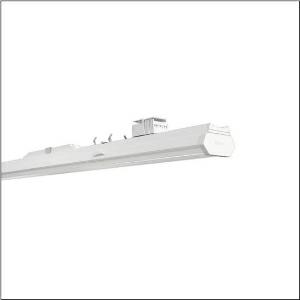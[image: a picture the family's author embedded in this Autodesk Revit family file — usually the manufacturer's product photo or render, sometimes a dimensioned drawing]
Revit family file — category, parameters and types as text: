
# Revit family: licross_21_protected_mo_52tp12dn4a5g3c
name_source: partatom
category: Lighting Fixtures
units: mm (PartAtom-declared; Revit-internal decimal feet)

## family parameters
Cut with Voids When Loaded = No
Host = Face
Light Source = No
Part Type = Normal
Room Calculation Point = No
Round Connector Dimension = Use Diameter
Shared = No

## types (1)
- --- (1 x LED, 940 lm, 6.8 W, 4000K)
    Apparent Load = 7 VA
    CIE Flux Codes = 73 92 98 99 100
    Color Rendering = 80
    Color Temperature = 4000K
    Default Elevation = 1800 mm
    Description = Licross 21 Protected MO, luminaire insert, of sheet steel, galvanised, coil coated, white, length: 1.500mm, width: 90mm, height: 103mm, LED rated luminous flux: 10.700lm, light colour: 840, SDCM (Standard Deviation of Colour Matching)MacAdam ≤ 3 SDCM (initial), control gear: DALI 2 (for two DALI lines), with plug, 6-pole, with phase selection, for trunking rail, 14-core, mains connection: 220..240V, AC, 50/60Hz, rated input power: 66W, for trunking rail, 14-core, internal wiring halogen-free, for emergency light function, converter,control gear: single battery element, battery: LiFePO4, 9Ah, primary light control with lens, of plastic, primary optical cover: cover, of PMMA, light emission: direct distribution, primary light characteristic: symmetric, protection rating (complete): IP64, insulation class (complete): insulation class I (protective earthing), certification: CE, UKCA, protection symbol: D if used in an environment with conductive dust loads with corresponding accessories, impact resistance: IK06, permissible ambient temperature for indoor applications: +5..+35°C, standard: EN 60598-2-22, LABS conformity tested according to VDMA 24364:2018-05, reducing of maximum allowable ambient temperature of 5°C with ceiling mounting, corresponds to IFS (International Featured Standards) requirements for safety and quality in the food industry, The light source and the operating device comply with the requirements of the Ecodesign Regulation (EU) 2019/2020 and are replaceable in accordance with this regulation, packaging unit: 1 piece
    Height = 92 mm
    Lamp = 1 x LED
    Lamp Light Flux = 940 lm
    Lamp Power = 6.8 W
    Lamp count = 1
    Length = 1500 mm
    Luminous efficacy = 138 lm/W
    Manufacturer = Siteco
    ModVariant = No
    Model = 52TP12DN4A5G3C
    Mounting Place = Ceiling
    Mounting Type = Pendant
    Number of Poles = 1
    OnlyDefault = Yes
    Power Factor = 1
    Product Name = Licross 21 Protected MO
    Product group = luminaire insert | ceiling pendant
    ProductGroupID = 901
    Protection Class = Protection class I
    Protection Degree = IP 64
    RLX_Detail_Level = 1
    RLX_Emergency_Light_Flux = 0 lm
    RLX_Emergency_Type = 0
    RLX_Emergency_Type_DB = No
    RlxData = <blob elided: 25189 chars, md5=a9f75ef8>
    Socket = socket
    Standby Power = 0 W
    System Light Flux = 940 lm
    System Power = 7 W
    Type Comments = : emergency light operation: 3 h
    Type Image = l_1256148.jpg
    URL = http://relux.com
    VarID = @adj_110877
    Voltage = 0 V
    Weight = 0.00 kg
    Width = 88 mm

## geometry (parser evidence)
native form markers: Blend x4, Sweep x9
no freeform markers — native parametric forms only
